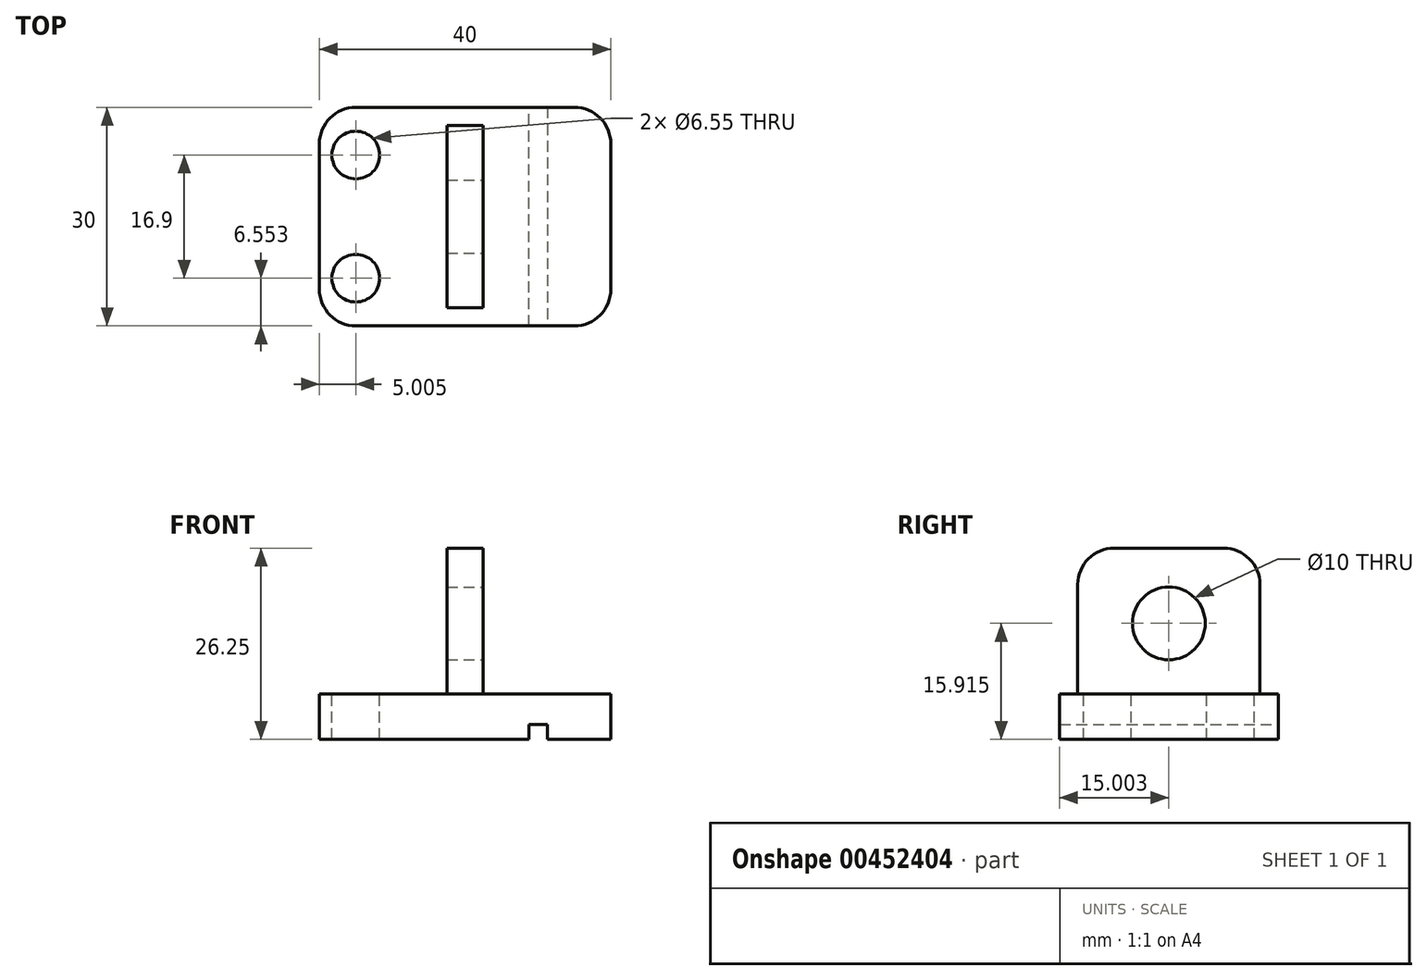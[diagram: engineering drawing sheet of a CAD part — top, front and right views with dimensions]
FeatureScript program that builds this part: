
annotation { "Feature Type Name" : "Feature", "Feature Type Description" : "" }
export const myFeature = defineFeature(function(context is Context, id is Id, definition is map)
    precondition{}
    {
        {
            var Q0;
            Q0=qCreatedBy(makeId("Top.planeOp"),FACE);
            var sketch = newSketch(context, id + "F0", { "sketchPlane" : qUnion([Q0])});
            skLineSegment(sketch, "E0.bottom", {"start": v(-18.73, 5.28) * mm, "end": v(21.27, 5.28) * mm});
            skLineSegment(sketch, "E0.top", {"start": v(-18.73, -24.72) * mm, "end": v(21.27, -24.72) * mm});
            skLineSegment(sketch, "E0.left", {"start": v(-18.73, 5.28) * mm, "end": v(-18.73, -24.72) * mm});
            skLineSegment(sketch, "E0.right", {"start": v(21.27, 5.28) * mm, "end": v(21.27, -24.72) * mm});
            skSolve(sketch);
        }
        {
            var Q0;
            Q0=makeQuery(id+"F0.imprint","IMPRINT",FACE,{"disambiguationData":[TD([[makeQuery(id+"F0.imprint","IMPRINT",EDGE,{"derivedFrom":sQuery(id+"F0.wireOp",EDGE,"E0.bottom")}),-1.0]])]});
            extrude(context, id + "F1", {"entities" : qUnion([Q0]), "depth" : 6.25 * mm});
        }
        {
            var Q0;
            Q0=makeQuery(id+"F1.opExtrude","SWEPT_EDGE",EDGE,{"disambiguationData":[OSD([sQuery(id+"F0.wireOp",EDGE,"E0.top"),sQuery(id+"F0.wireOp",EDGE,"E0.left")])]});
            var Q1;
            Q1=makeQuery(id+"F1.opExtrude","SWEPT_EDGE",EDGE,{"disambiguationData":[OSD([sQuery(id+"F0.wireOp",EDGE,"E0.top"),sQuery(id+"F0.wireOp",EDGE,"E0.right")])]});
            var Q2;
            Q2=makeQuery(id+"F1.opExtrude","SWEPT_EDGE",EDGE,{"disambiguationData":[OSD([sQuery(id+"F0.wireOp",EDGE,"E0.bottom"),sQuery(id+"F0.wireOp",EDGE,"E0.right")])]});
            var Q3;
            Q3=makeQuery(id+"F1.opExtrude","SWEPT_EDGE",EDGE,{"disambiguationData":[OSD([sQuery(id+"F0.wireOp",EDGE,"E0.bottom"),sQuery(id+"F0.wireOp",EDGE,"E0.left")])]});
            fillet(context, id + "F2", {"entities" : qUnion([Q0, Q1, Q2, Q3]), "radius" : 5 * mm, "tangentPropagation" : true, "allowEdgeOverflow" : false});
        }
        {
            var Q0;
            Q0=makeQuery(id+"F1.opExtrude","CAP_FACE",FACE,{"disambiguationData":[OSD([sQuery(id+"F0.wireOp",EDGE,"E0.bottom"),sQuery(id+"F0.wireOp",EDGE,"E0.top"),sQuery(id+"F0.wireOp",EDGE,"E0.left"),sQuery(id+"F0.wireOp",EDGE,"E0.right")])],"isStart":false});
            var sketch = newSketch(context, id + "F3", { "sketchPlane" : qUnion([Q0])});
            skLineSegment(sketch, "E1", {"start": v(-18.73, -3.88) * mm, "end": v(-1.23, -3.88) * mm, "construction": true});
            skLineSegment(sketch, "E2", {"start": v(-1.23, -3.88) * mm, "end": v(3.77, -3.88) * mm, "construction": true});
            skLineSegment(sketch, "E3", {"start": v(3.77, -3.88) * mm, "end": v(21.27, -3.88) * mm, "construction": true});
            skLineSegment(sketch, "E4", {"start": v(0.54, 5.28) * mm, "end": v(0.54, 2.78) * mm, "construction": true});
            skLineSegment(sketch, "E5", {"start": v(0.54, 2.78) * mm, "end": v(0.54, -22.22) * mm, "construction": true});
            skLineSegment(sketch, "E6", {"start": v(0.54, -22.22) * mm, "end": v(0.54, -24.72) * mm, "construction": true});
            skPoint(sketch, "E6.endSnap0", {"position": v(1.27, -24.72) * mm});
            skLineSegment(sketch, "E7.bottom", {"start": v(3.77, 2.78) * mm, "end": v(-1.23, 2.78) * mm});
            skLineSegment(sketch, "E7.top", {"start": v(3.77, -22.22) * mm, "end": v(-1.23, -22.22) * mm});
            skLineSegment(sketch, "E7.left", {"start": v(3.77, 2.78) * mm, "end": v(3.77, -22.22) * mm});
            skLineSegment(sketch, "E7.right", {"start": v(-1.23, 2.78) * mm, "end": v(-1.23, -22.22) * mm});
            skSolve(sketch);
        }
        {
            var Q0;
            Q0=makeQuery(id+"F3.imprint","IMPRINT",FACE,{"disambiguationData":[TD([[makeQuery(id+"F3.imprint","IMPRINT",EDGE,{"derivedFrom":sQuery(id+"F3.wireOp",EDGE,"E7.bottom")}),1.0]])]});
            extrude(context, id + "F4", {"entities" : qUnion([Q0]), "operationType" : NewBodyOperationType.ADD, "depth" : 20 * mm});
        }
        {
            var Q0;
            Q0=makeQuery(id+"F4.opExtrude","CAP_EDGE",EDGE,{"disambiguationData":[OSD([sQuery(id+"F3.wireOp",EDGE,"E7.top")])],"isStart":true});
            var Q1;
            Q1=makeQuery(id+"F4.opExtrude","CAP_EDGE",EDGE,{"disambiguationData":[OSD([sQuery(id+"F3.wireOp",EDGE,"E7.top")])],"isStart":false});
            var Q2;
            Q2=makeQuery(id+"F4.opExtrude","CAP_EDGE",EDGE,{"disambiguationData":[OSD([sQuery(id+"F3.wireOp",EDGE,"E7.bottom")])],"isStart":false});
            var Q3;
            Q3=makeQuery(id+"F4.opExtrude","CAP_EDGE",EDGE,{"disambiguationData":[OSD([sQuery(id+"F3.wireOp",EDGE,"E7.bottom")])],"isStart":true});
            fillet(context, id + "F5", {"entities" : qUnion([Q0, Q1, Q2, Q3]), "radius" : 5 * mm, "tangentPropagation" : true, "allowEdgeOverflow" : false});
        }
        {
            var Q0;
            Q0=makeQuery(id+"F5.opFillet","SPLIT",FACE,{"disambiguationData":[OD(0.0)],"derivedFrom":makeQuery(id+"F1.opExtrude","CAP_FACE",FACE,{"disambiguationData":[OSD([sQuery(id+"F0.wireOp",EDGE,"E0.bottom"),sQuery(id+"F0.wireOp",EDGE,"E0.top"),sQuery(id+"F0.wireOp",EDGE,"E0.left"),sQuery(id+"F0.wireOp",EDGE,"E0.right")])],"isStart":false})});
            var sketch = newSketch(context, id + "F6", { "sketchPlane" : qUnion([Q0])});
            skLineSegment(sketch, "E8", {"start": v(-13.73, 5.28) * mm, "end": v(-13.73, -1.27) * mm, "construction": true});
            skLineSegment(sketch, "E9", {"start": v(-13.73, -1.27) * mm, "end": v(-13.73, -18.17) * mm, "construction": true});
            skLineSegment(sketch, "E10", {"start": v(-13.73, -18.17) * mm, "end": v(-13.73, -24.72) * mm, "construction": true});
            skCircle(sketch, "E11", {"center": v(-13.73, -18.17) * mm, "radius": 3.28 * mm});
            skCircle(sketch, "E12", {"center": v(-13.73, -1.27) * mm, "radius": 3.28 * mm});
            skSolve(sketch);
        }
        {
            var Q0;
            Q0=makeQuery(id+"F4.opExtrude","SWEPT_FACE",FACE,{"disambiguationData":[OSD([sQuery(id+"F3.wireOp",EDGE,"E7.left")])]});
            var sketch = newSketch(context, id + "F7", { "sketchPlane" : qUnion([Q0])});
            skLineSegment(sketch, "E13", {"start": v(-22.22, 15.92) * mm, "end": v(-9.72, 15.92) * mm, "construction": true});
            skCircle(sketch, "E14", {"center": v(-9.72, 15.92) * mm, "radius": 5 * mm});
            skSolve(sketch);
        }
        {
            var Q0;
            Q0=makeQuery(id+"F7.imprint","IMPRINT",FACE,{"disambiguationData":[TD([[makeQuery(id+"F7.imprint","IMPRINT",EDGE,{"derivedFrom":sQuery(id+"F7.wireOp",EDGE,"E14")}),1.0]])]});
            extrude(context, id + "F8", {"entities" : qUnion([Q0]), "operationType" : NewBodyOperationType.REMOVE, "oppositeDirection" : true, "depth" : 5 * mm});
        }
        {
            var Q0;
            Q0=makeQuery(id+"F6.imprint","IMPRINT",FACE,{"disambiguationData":[TD([[makeQuery(id+"F6.imprint","IMPRINT",EDGE,{"derivedFrom":sQuery(id+"F6.wireOp",EDGE,"E12")}),1.0]])]});
            var Q1;
            Q1=makeQuery(id+"F6.imprint","IMPRINT",FACE,{"disambiguationData":[TD([[makeQuery(id+"F6.imprint","IMPRINT",EDGE,{"derivedFrom":sQuery(id+"F6.wireOp",EDGE,"E11")}),1.0]])]});
            extrude(context, id + "F9", {"entities" : qUnion([Q0, Q1]), "operationType" : NewBodyOperationType.REMOVE, "oppositeDirection" : true, "depth" : 25 * mm});
        }
        {
            var Q0;
            Q0=makeQuery(id+"F1.opExtrude","CAP_FACE",FACE,{"disambiguationData":[OSD([sQuery(id+"F0.wireOp",EDGE,"E0.bottom"),sQuery(id+"F0.wireOp",EDGE,"E0.top"),sQuery(id+"F0.wireOp",EDGE,"E0.left"),sQuery(id+"F0.wireOp",EDGE,"E0.right")])],"isStart":true});
            var sketch = newSketch(context, id + "F10", { "sketchPlane" : qUnion([Q0])});
            skLineSegment(sketch, "E15", {"start": v(21.27, 17.7) * mm, "end": v(12.52, 17.7) * mm, "construction": true});
            skLineSegment(sketch, "E16", {"start": v(12.52, 17.7) * mm, "end": v(10.02, 17.7) * mm, "construction": true});
            skLineSegment(sketch, "E17", {"start": v(10.06, 24.72) * mm, "end": v(10.06, -5.28) * mm});
            skLineSegment(sketch, "E18", {"start": v(10.06, -5.28) * mm, "end": v(12.56, -5.28) * mm});
            skLineSegment(sketch, "E19", {"start": v(12.56, -5.28) * mm, "end": v(12.56, 24.72) * mm});
            skLineSegment(sketch, "E20", {"start": v(12.56, 24.72) * mm, "end": v(10.06, 24.72) * mm});
            skSolve(sketch);
        }
        {
            var Q0;
            Q0=makeQuery(id+"F10.imprint","IMPRINT",FACE,{"disambiguationData":[TD([[makeQuery(id+"F10.imprint","IMPRINT",EDGE,{"derivedFrom":sQuery(id+"F10.wireOp",EDGE,"E17")}),1.0]])]});
            extrude(context, id + "F11", {"entities" : qUnion([Q0]), "operationType" : NewBodyOperationType.REMOVE, "oppositeDirection" : true, "depth" : 2 * mm});
        }
    });
